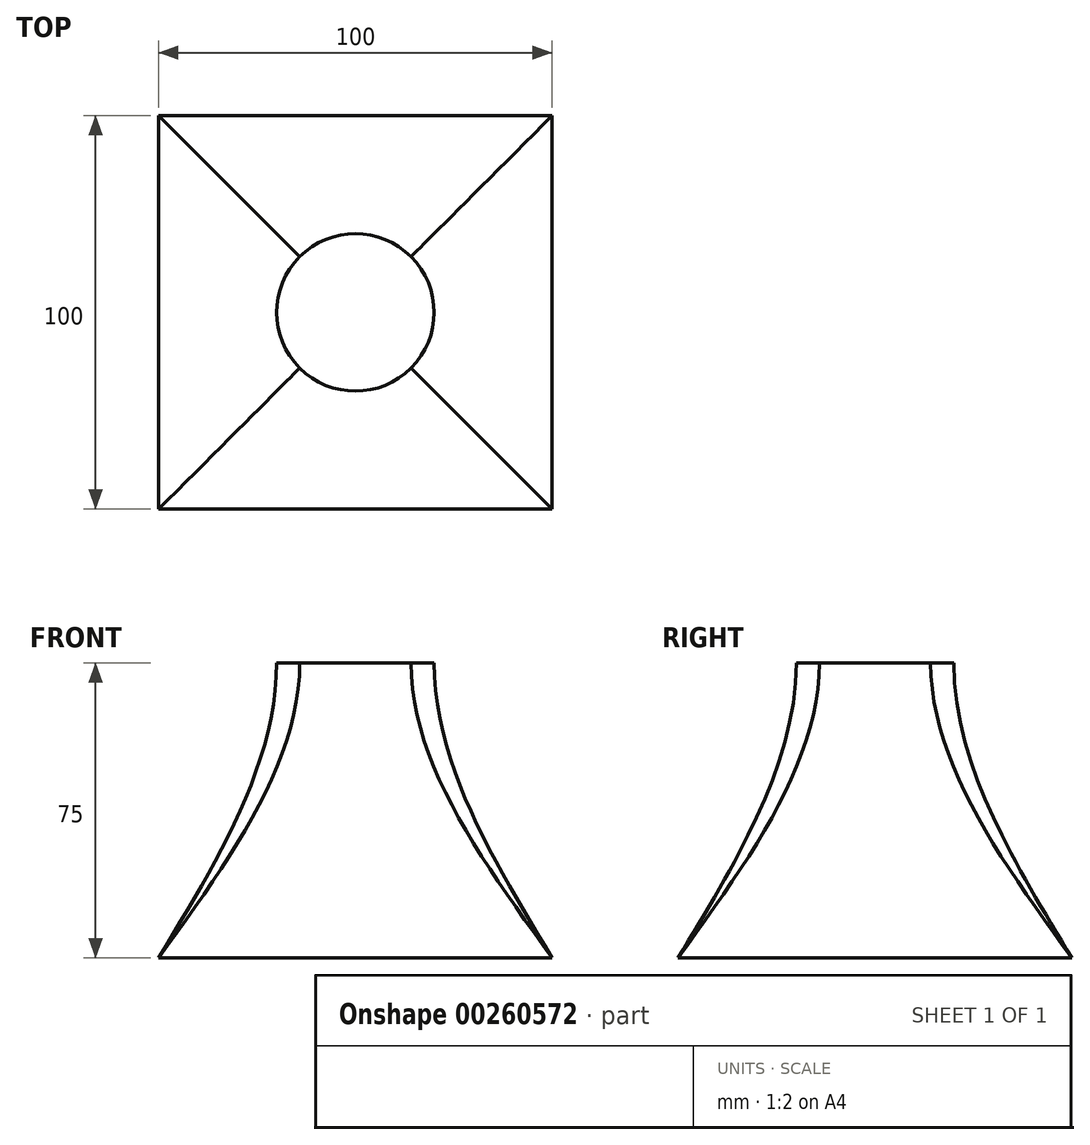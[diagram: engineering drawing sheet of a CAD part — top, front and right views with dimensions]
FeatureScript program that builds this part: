
annotation { "Feature Type Name" : "Feature", "Feature Type Description" : "" }
export const myFeature = defineFeature(function(context is Context, id is Id, definition is map)
    precondition{}
    {
        {
            var Q0;
            Q0=qCreatedBy(makeId("Top.planeOp"),FACE);
            var sketch = newSketch(context, id + "F0", { "sketchPlane" : qUnion([Q0])});
            skLineSegment(sketch, "E0.bottom", {"start": v(-50, 50) * mm, "end": v(50, 50) * mm});
            skLineSegment(sketch, "E0.top", {"start": v(-50, -50) * mm, "end": v(50, -50) * mm});
            skLineSegment(sketch, "E0.left", {"start": v(-50, 50) * mm, "end": v(-50, -50) * mm});
            skLineSegment(sketch, "E0.right", {"start": v(50, 50) * mm, "end": v(50, -50) * mm});
            skPoint(sketch, "E0.middle", {"position": v(0, 0) * mm});
            skSolve(sketch);
        }
        {
            var Q0;
            Q0=makeQuery(id+"F0.imprint","IMPRINT",FACE,{"disambiguationData":[TD([[makeQuery(id+"F0.imprint","IMPRINT",EDGE,{"derivedFrom":sQuery(id+"F0.wireOp",EDGE,"E0.bottom")}),-1.0]])]});
            cPlane(context, id + "F1", {"entities" : qUnion([Q0]), "cplaneType" : CPlaneType.OFFSET, "offset" : 75 * mm, "width" : 150 * mm, "height" : 150 * mm});
        }
        {
            var Q0;
            Q0=qCreatedBy(id+"F1.planeOp",FACE);
            var sketch = newSketch(context, id + "F2", { "sketchPlane" : qUnion([Q0])});
            skCircle(sketch, "E1", {"center": v(0, 0) * mm, "radius": 20 * mm});
            skSolve(sketch);
        }
        {
            var Q0;
            Q0=makeQuery(id+"F2.imprint","IMPRINT",FACE,{"disambiguationData":[TD([[makeQuery(id+"F2.imprint","IMPRINT",EDGE,{"derivedFrom":sQuery(id+"F2.wireOp",EDGE,"E1")}),1.0]])]});
            var Q1;
            Q1=makeQuery(id+"F0.imprint","IMPRINT",FACE,{"disambiguationData":[TD([[makeQuery(id+"F0.imprint","IMPRINT",EDGE,{"derivedFrom":sQuery(id+"F0.wireOp",EDGE,"E0.bottom")}),-1.0]])]});
            loft(context, id + "F3", {"startCondition" : LoftEndDerivativeType.NORMAL_TO_PROFILE, "startMagnitude" : 1, "sheetProfilesArray" : [{ "sheetProfileEntities" : qUnion([Q0]) }, { "sheetProfileEntities" : qUnion([Q1]) }]});
        }
    });
